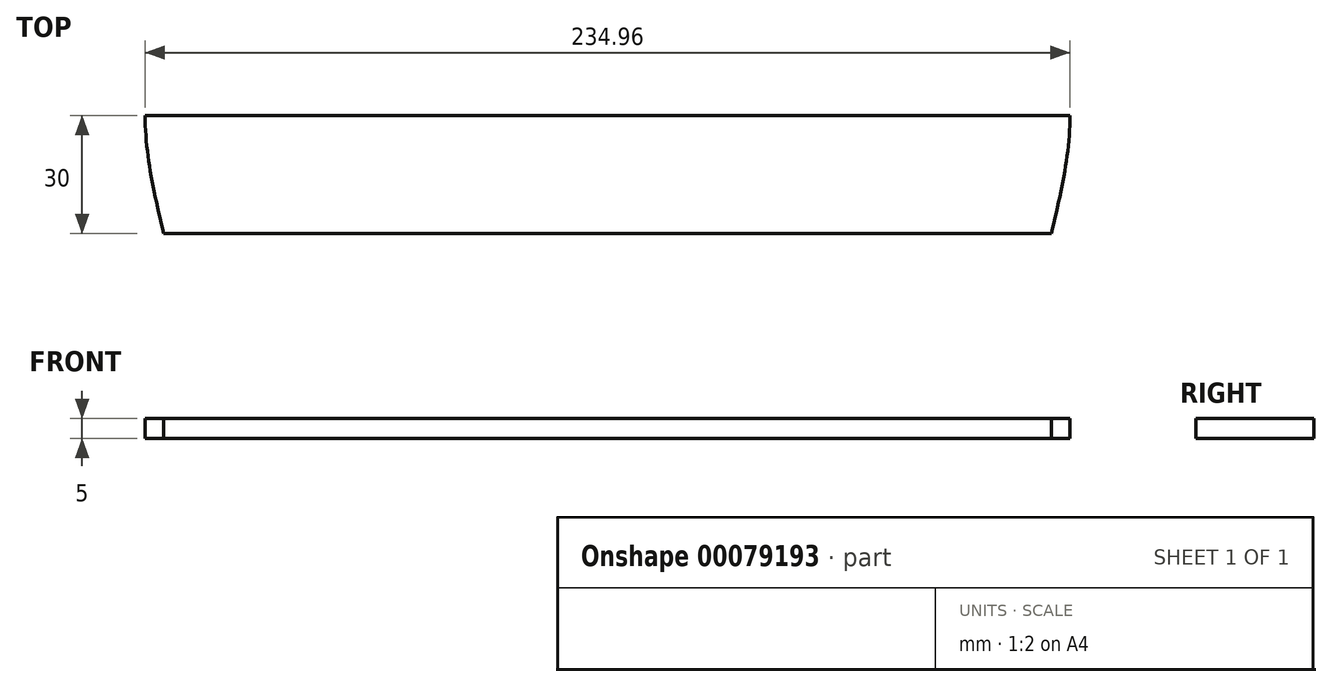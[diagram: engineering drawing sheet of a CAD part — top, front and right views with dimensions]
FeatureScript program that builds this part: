
annotation { "Feature Type Name" : "Feature", "Feature Type Description" : "" }
export const myFeature = defineFeature(function(context is Context, id is Id, definition is map)
    precondition{}
    {
        {
            var Q0;
            Q0=qCreatedBy(makeId("Top.planeOp"),FACE);
            var sketch = newSketch(context, id + "F0", { "sketchPlane" : qUnion([Q0])});
            skPoint(sketch, "E0", {"position": v(120.55, -132.94) * mm});
            skPoint(sketch, "E1", {"position": v(86.1, -177.7) * mm});
            skPoint(sketch, "E2", {"position": v(55.36, -169.8) * mm});
            skPoint(sketch, "E3", {"position": v(0, -197.44) * mm});
            skPoint(sketch, "E4", {"position": v(110.71, -142.15) * mm});
            skPoint(sketch, "E5", {"position": v(117.48, 0) * mm});
            skPoint(sketch, "E6", {"position": v(106.4, -66.47) * mm});
            skLineSegment(sketch, "E7", {"start": v(0, 292) * mm, "end": v(0, -197.44) * mm, "construction": true});
            skPoint(sketch, "E8.MirrorP", {"position": v(-117.48, 0) * mm});
            skPoint(sketch, "E9.MirrorP", {"position": v(-106.4, -66.47) * mm});
            skPoint(sketch, "E10.MirrorP", {"position": v(-120.55, -132.94) * mm});
            skPoint(sketch, "E11.MirrorP", {"position": v(-110.71, -142.15) * mm});
            skPoint(sketch, "E12.MirrorP", {"position": v(-86.1, -177.7) * mm});
            skPoint(sketch, "E13.MirrorP", {"position": v(-55.36, -169.8) * mm});
            skPoint(sketch, "E14", {"position": v(0, 0) * mm});
            skPoint(sketch, "E15", {"position": v(-117.3, -129.45) * mm});
            skPoint(sketch, "E16", {"position": v(-109.77, -151.8) * mm});
            skPoint(sketch, "E17", {"position": v(-117.3, -138.2) * mm});
            skPoint(sketch, "E18", {"position": v(-105.1, -168.47) * mm});
            skPoint(sketch, "E19", {"position": v(-76.04, -175.14) * mm});
            skPoint(sketch, "E20", {"position": v(-48.6, -178.72) * mm});
            skPoint(sketch, "E21", {"position": v(-53.93, -172.02) * mm});
            skPoint(sketch, "E22", {"position": v(-58.13, -168.59) * mm});
            skPoint(sketch, "E23", {"position": v(-95.73, -175.68) * mm});
            skPoint(sketch, "E24", {"position": v(-120.2, -134.48) * mm});
            skPoint(sketch, "E25.MirrorP", {"position": v(48.6, -178.72) * mm});
            skPoint(sketch, "E26.MirrorP", {"position": v(53.93, -172.02) * mm});
            skPoint(sketch, "E27.MirrorP", {"position": v(58.13, -168.59) * mm});
            skPoint(sketch, "E28.MirrorP", {"position": v(76.04, -175.14) * mm});
            skPoint(sketch, "E29.MirrorP", {"position": v(95.73, -175.68) * mm});
            skPoint(sketch, "E30.MirrorP", {"position": v(109.77, -151.8) * mm});
            skPoint(sketch, "E31.MirrorP", {"position": v(117.3, -138.2) * mm});
            skPoint(sketch, "E32.MirrorP", {"position": v(120.2, -134.48) * mm});
            skPoint(sketch, "E33.MirrorP", {"position": v(117.3, -129.45) * mm});
            skPoint(sketch, "E34", {"position": v(-112.06, -140.6) * mm});
            skPoint(sketch, "E35.MirrorP", {"position": v(105.1, -168.47) * mm});
            skPoint(sketch, "E36.MirrorP", {"position": v(-106.4, 66.47) * mm});
            skPoint(sketch, "E37.MirrorP", {"position": v(-112.06, 140.6) * mm});
            skPoint(sketch, "E38.MirrorP", {"position": v(-120.55, 132.94) * mm});
            skPoint(sketch, "E39.MirrorP", {"position": v(55.36, 169.8) * mm});
            skPoint(sketch, "E40.MirrorP", {"position": v(120.55, 132.94) * mm});
            skPoint(sketch, "E41.MirrorP", {"position": v(-53.93, 172.02) * mm});
            skPoint(sketch, "E42.MirrorP", {"position": v(105.1, 168.47) * mm});
            skPoint(sketch, "E43.MirrorP", {"position": v(48.6, 178.72) * mm});
            skPoint(sketch, "E44.MirrorP", {"position": v(95.73, 175.68) * mm});
            skPoint(sketch, "E45.MirrorP", {"position": v(109.77, 151.8) * mm});
            skPoint(sketch, "E46.MirrorP", {"position": v(-58.13, 168.59) * mm});
            skPoint(sketch, "E47.MirrorP", {"position": v(-110.71, 142.15) * mm});
            skPoint(sketch, "E48.MirrorP", {"position": v(-55.36, 169.8) * mm});
            skPoint(sketch, "E49.MirrorP", {"position": v(58.13, 168.59) * mm});
            skPoint(sketch, "E50.MirrorP", {"position": v(-117.3, 129.45) * mm});
            skPoint(sketch, "E51.MirrorP", {"position": v(-109.77, 151.8) * mm});
            skPoint(sketch, "E52.MirrorP", {"position": v(110.71, 142.15) * mm});
            skPoint(sketch, "E53.MirrorP", {"position": v(53.93, 172.02) * mm});
            skPoint(sketch, "E54.MirrorP", {"position": v(-120.2, 134.48) * mm});
            skPoint(sketch, "E55.MirrorP", {"position": v(120.2, 134.48) * mm});
            skPoint(sketch, "E56.MirrorP", {"position": v(-86.1, 177.7) * mm});
            skPoint(sketch, "E57.MirrorP", {"position": v(-76.04, 175.14) * mm});
            skPoint(sketch, "E58.MirrorP", {"position": v(117.3, 138.2) * mm});
            skPoint(sketch, "E59.MirrorP", {"position": v(86.1, 177.7) * mm});
            skPoint(sketch, "E60.MirrorP", {"position": v(-105.1, 168.47) * mm});
            skPoint(sketch, "E61.MirrorP", {"position": v(76.04, 175.14) * mm});
            skPoint(sketch, "E62.MirrorP", {"position": v(117.3, 129.45) * mm});
            skPoint(sketch, "E63.MirrorP", {"position": v(0, 197.44) * mm});
            skPoint(sketch, "E64.MirrorP", {"position": v(-117.3, 138.2) * mm});
            skPoint(sketch, "E65.MirrorP", {"position": v(-95.73, 175.68) * mm});
            skPoint(sketch, "E66.MirrorP", {"position": v(-48.6, 178.72) * mm});
            skPoint(sketch, "E67.MirrorP", {"position": v(106.4, 66.47) * mm});
            skFitSpline(sketch, "E68", {"points": [v(-117.48, 0) * mm, v(-106.4, 66.47) * mm, v(-117.3, 129.45) * mm, v(-120.55, 132.94) * mm, v(-120.2, 134.48) * mm, v(-117.3, 138.2) * mm, v(-112.06, 140.6) * mm, v(-110.71, 142.15) * mm, v(-109.77, 151.8) * mm, v(-105.1, 168.47) * mm, v(-95.73, 175.68) * mm, v(-86.1, 177.7) * mm, v(-76.04, 175.14) * mm, v(-58.13, 168.59) * mm, v(-55.36, 169.8) * mm, v(-53.93, 172.02) * mm, v(-48.6, 178.72) * mm, v(0, 197.44) * mm, v(48.6, 178.72) * mm, v(53.93, 172.02) * mm, v(55.36, 169.8) * mm, v(58.13, 168.59) * mm, v(76.04, 175.14) * mm, v(86.1, 177.7) * mm, v(95.73, 175.68) * mm, v(105.1, 168.47) * mm, v(109.77, 151.8) * mm, v(110.71, 142.15) * mm, v(117.3, 138.2) * mm, v(120.2, 134.48) * mm, v(120.55, 132.94) * mm, v(117.3, 129.45) * mm, v(106.4, 66.47) * mm, v(117.48, 0) * mm, v(106.4, -66.47) * mm, v(117.3, -129.45) * mm, v(120.55, -132.94) * mm, v(120.2, -134.48) * mm, v(117.3, -138.2) * mm, v(110.71, -142.15) * mm, v(109.77, -151.8) * mm, v(105.1, -168.47) * mm, v(95.73, -175.68) * mm, v(86.1, -177.7) * mm, v(76.04, -175.14) * mm, v(58.13, -168.59) * mm, v(55.36, -169.8) * mm, v(53.93, -172.02) * mm, v(48.6, -178.72) * mm, v(0, -197.44) * mm, v(-48.6, -178.72) * mm, v(-53.93, -172.02) * mm, v(-55.36, -169.8) * mm, v(-58.13, -168.59) * mm, v(-76.04, -175.14) * mm, v(-86.1, -177.7) * mm, v(-95.73, -175.68) * mm, v(-105.1, -168.47) * mm, v(-109.77, -151.8) * mm, v(-110.71, -142.15) * mm, v(-112.06, -140.6) * mm, v(-117.3, -138.2) * mm, v(-120.2, -134.48) * mm, v(-120.55, -132.94) * mm, v(-117.3, -129.45) * mm, v(-106.4, -66.47) * mm, v(-117.48, 0) * mm]});
            skPoint(sketch, "E69", {"position": v(0, 295) * mm});
            skPoint(sketch, "E70", {"position": v(-30, 295) * mm});
            skPoint(sketch, "E71", {"position": v(-225, 0) * mm});
            skPoint(sketch, "E72", {"position": v(-225, 100) * mm});
            skPoint(sketch, "E73.MirrorP", {"position": v(225, 100) * mm});
            skPoint(sketch, "E74.MirrorP", {"position": v(225, -60) * mm});
            skLineSegment(sketch, "E75", {"start": v(0, 0) * mm, "end": v(-373.3, 215.53) * mm, "construction": true});
            skLineSegment(sketch, "E76", {"start": v(0, 0) * mm, "end": v(-204.64, 354.44) * mm, "construction": true});
            skLineSegment(sketch, "E77", {"start": v(-225, 0) * mm, "end": v(-225, 100) * mm});
            skLineSegment(sketch, "E78", {"start": v(-30, 295) * mm, "end": v(0, 295) * mm});
            skPoint(sketch, "E79", {"position": v(-30, 100) * mm});
            skArc(sketch, "E80", {"start": v(-30, 295) * mm, "mid": v(-167.89, 237.89) * mm, "end": v(-225, 100) * mm});
            skLineSegment(sketch, "E81.MirrorCS", {"start": v(225, 0) * mm, "end": v(225, 100) * mm});
            skArc(sketch, "E82.MirrorCS", {"start": v(30, 295) * mm, "mid": v(167.89, 237.89) * mm, "end": v(225, 100) * mm});
            skLineSegment(sketch, "E83.MirrorCS", {"start": v(30, 295) * mm, "end": v(0, 295) * mm});
            skArc(sketch, "E84.MirrorCS", {"start": v(-30, -295) * mm, "mid": v(-167.89, -237.89) * mm, "end": v(-225, -100) * mm});
            skLineSegment(sketch, "E85.MirrorCS", {"start": v(-225, 0) * mm, "end": v(-225, -100) * mm});
            skLineSegment(sketch, "E86.MirrorCS", {"start": v(225, 0) * mm, "end": v(225, -100) * mm});
            skArc(sketch, "E87.MirrorCS", {"start": v(30, -295) * mm, "mid": v(167.89, -237.89) * mm, "end": v(225, -100) * mm});
            skLineSegment(sketch, "E88.MirrorCS", {"start": v(30, -295) * mm, "end": v(0, -295) * mm});
            skLineSegment(sketch, "E89.MirrorCS", {"start": v(-30, -295) * mm, "end": v(0, -295) * mm});
            skLineSegment(sketch, "E90", {"start": v(-254.05, 0) * mm, "end": v(241.92, 0) * mm});
            skLineSegment(sketch, "E91.0", {"start": v(-254.05, -30) * mm, "end": v(-225, -30) * mm});
            skLineSegment(sketch, "E92.trimOffspring", {"start": v(-112.75, -30) * mm, "end": v(112.75, -30) * mm});
            skLineSegment(sketch, "E93.trimOffspring", {"start": v(225, -30) * mm, "end": v(241.92, -30) * mm});
            skSolve(sketch);
        }
        {
            var Q0;
            Q0=makeQuery(id+"F0.imprint","IMPRINT",FACE,{"disambiguationData":[TD([[makeQuery(id+"F0.imprint","IMPRINT",EDGE,{"derivedFrom":sQuery(id+"F0.wireOp",EDGE,"E68")}),-1.0]])]});
            extrude(context, id + "F1", {"entities" : qUnion([Q0]), "depth" : 5 * mm, "offsetDistance" : 25 * mm, "symmetric" : true});
        }
        {
            var Q0;
            Q0=makeQuery(id+"F1.opExtrude","CAP_FACE",FACE,{"disambiguationData":[OSD([sQuery(id+"F0.wireOp",EDGE,"E68"),sQuery(id+"F0.wireOp",EDGE,"E92.trimOffspring")])],"isStart":false});
            cPlane(context, id + "F2", {"entities" : qUnion([Q0]), "cplaneType" : CPlaneType.OFFSET, "offset" : 50 * mm, "width" : 150 * mm, "height" : 150 * mm});
        }
    });
